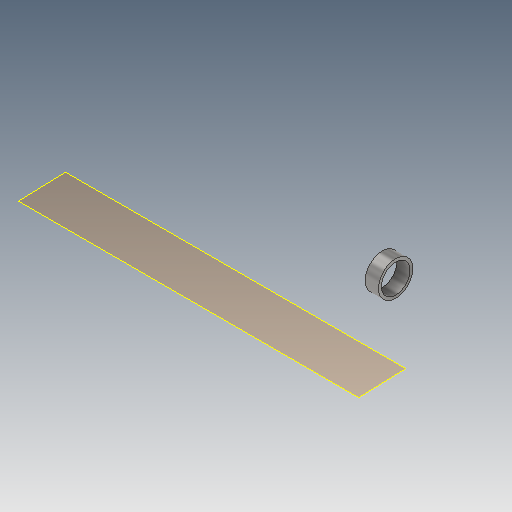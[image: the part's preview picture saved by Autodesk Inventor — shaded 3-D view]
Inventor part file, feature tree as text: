
AUTODESK INVENTOR PART (.ipt)
format: ipt  version: 2025 (Build 290162000, 162)  size: 97,280 bytes
history: native  units: mm
features: other x5, reference x3, plane x1, revolve x1, sketch x1
ambient origin geometry x8: Origin, YZ Plane, XZ Plane, XY Plane, X Axis, Y Axis, Z Axis, Center Point
bodies: 实体1 (feature_tree)
feature tree (11):
  plane  "工作平面1"
  revolve  "旋转1"  Angle=90.0deg
  sketch  "草图1"  dims[d0=18.0mm d1=90.0deg]
  reference  "参考1"
  reference  "参考2"
  reference  "参考3"
  other  "齿轮箱.iam"
  other  "高速轴:1"
  other  "轴承:1"
  other  "滚动轴承 GB/T 276-1994 60000 和 160000 型 6206:1"
  other  "轴:1"
